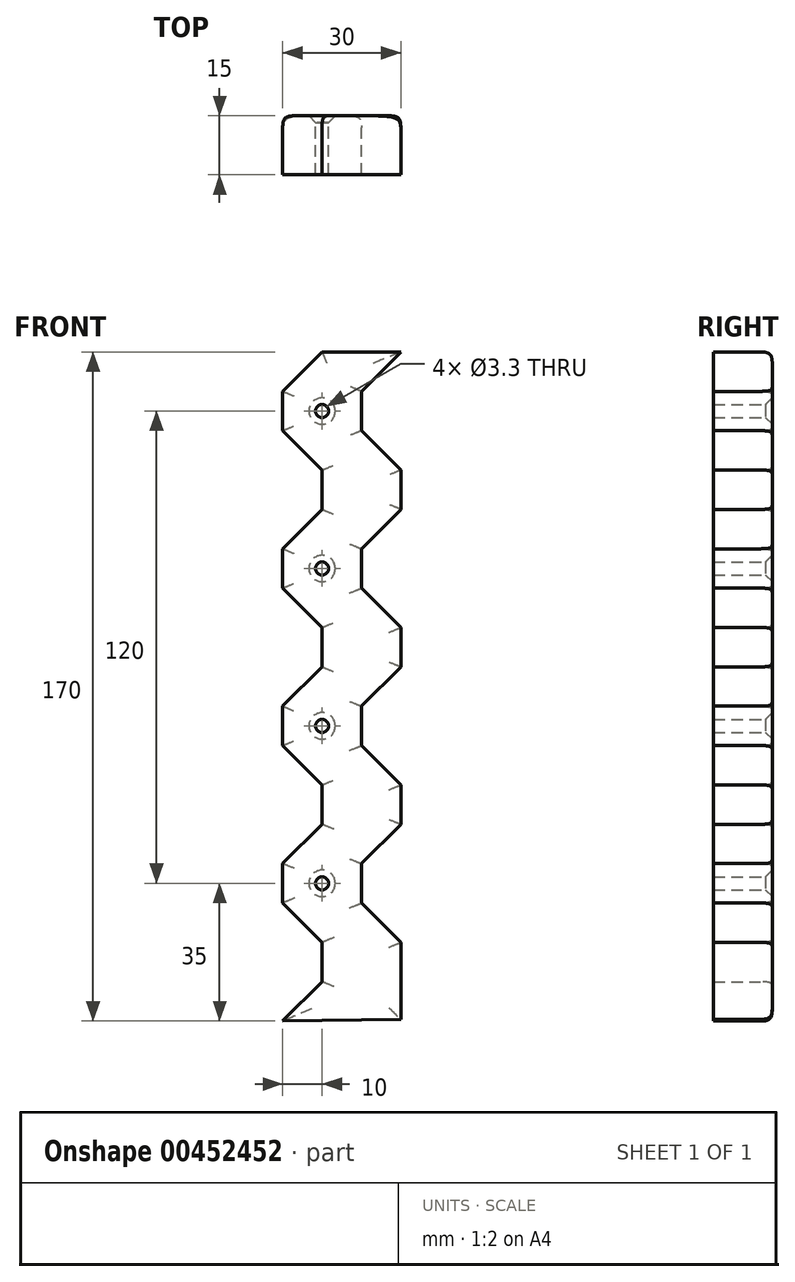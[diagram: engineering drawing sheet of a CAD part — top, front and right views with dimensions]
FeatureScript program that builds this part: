
annotation { "Feature Type Name" : "Feature", "Feature Type Description" : "" }
export const myFeature = defineFeature(function(context is Context, id is Id, definition is map)
    precondition{}
    {
        {
            var Q0;
            Q0=qCreatedBy(makeId("Front.planeOp"),FACE);
            var sketch = newSketch(context, id + "F0", { "sketchPlane" : qUnion([Q0])});
            skLineSegment(sketch, "E0", {"start": v(0, 0) * mm, "end": v(-5, 0) * mm});
            skLineSegment(sketch, "E1", {"start": v(-5, 0) * mm, "end": v(-15, 0) * mm});
            skLineSegment(sketch, "E2", {"start": v(0, 0) * mm, "end": v(5, 0) * mm});
            skLineSegment(sketch, "E3", {"start": v(5, 0) * mm, "end": v(15, 0) * mm});
            skLineSegment(sketch, "E4", {"start": v(-15, 0) * mm, "end": v(-15, -10) * mm});
            skLineSegment(sketch, "E5", {"start": v(-15, -10) * mm, "end": v(-15, -20) * mm});
            skLineSegment(sketch, "E6", {"start": v(-15, -20) * mm, "end": v(-15, -30) * mm});
            skLineSegment(sketch, "E7", {"start": v(-15, -30) * mm, "end": v(-15, -40) * mm});
            skLineSegment(sketch, "E8", {"start": v(-15, -40) * mm, "end": v(-15, -50) * mm});
            skLineSegment(sketch, "E9", {"start": v(-15, -60) * mm, "end": v(-15, -50) * mm});
            skLineSegment(sketch, "E10", {"start": v(-5, 0) * mm, "end": v(-5, -170) * mm});
            skLineSegment(sketch, "E11", {"start": v(-15, -60) * mm, "end": v(-15, -70) * mm});
            skLineSegment(sketch, "E12", {"start": v(-15, -70) * mm, "end": v(-15, -80) * mm});
            skLineSegment(sketch, "E13", {"start": v(-15, -80) * mm, "end": v(-15, -90) * mm});
            skLineSegment(sketch, "E14", {"start": v(-15, -90) * mm, "end": v(-15, -100) * mm});
            skLineSegment(sketch, "E15", {"start": v(-15, -100) * mm, "end": v(-15, -110) * mm});
            skLineSegment(sketch, "E16", {"start": v(-15, -110) * mm, "end": v(-15, -120) * mm});
            skLineSegment(sketch, "E17", {"start": v(-15, -120) * mm, "end": v(-15, -130) * mm});
            skLineSegment(sketch, "E18", {"start": v(-15, -130) * mm, "end": v(-15, -140) * mm});
            skLineSegment(sketch, "E19", {"start": v(-15, -140) * mm, "end": v(-15, -150) * mm});
            skLineSegment(sketch, "E20", {"start": v(-15, -150) * mm, "end": v(-15, -160) * mm});
            skLineSegment(sketch, "E21", {"start": v(-15, -160) * mm, "end": v(-15, -170) * mm});
            skLineSegment(sketch, "E22", {"start": v(5, 0) * mm, "end": v(5, -169.57) * mm});
            skLineSegment(sketch, "E23", {"start": v(15, 0) * mm, "end": v(15, -169.57) * mm});
            skLineSegment(sketch, "E24", {"start": v(-15, -10) * mm, "end": v(15, -10) * mm});
            skLineSegment(sketch, "E25", {"start": v(-15, -20) * mm, "end": v(15, -20) * mm});
            skLineSegment(sketch, "E26", {"start": v(-15, -30) * mm, "end": v(15, -30) * mm});
            skLineSegment(sketch, "E27", {"start": v(-15, -40) * mm, "end": v(15, -40) * mm});
            skLineSegment(sketch, "E28", {"start": v(-15, -50) * mm, "end": v(15, -50) * mm});
            skLineSegment(sketch, "E29", {"start": v(-15, -60) * mm, "end": v(15, -60) * mm});
            skLineSegment(sketch, "E30", {"start": v(-15, -70) * mm, "end": v(15, -70) * mm});
            skLineSegment(sketch, "E31", {"start": v(-15, -80) * mm, "end": v(15, -80) * mm});
            skLineSegment(sketch, "E32", {"start": v(-15, -90) * mm, "end": v(15, -90) * mm});
            skLineSegment(sketch, "E33", {"start": v(-15, -100) * mm, "end": v(15, -100) * mm});
            skLineSegment(sketch, "E34", {"start": v(-15, -110) * mm, "end": v(15, -110) * mm});
            skLineSegment(sketch, "E35", {"start": v(-15, -120) * mm, "end": v(15, -120) * mm});
            skLineSegment(sketch, "E36", {"start": v(-15, -130) * mm, "end": v(15, -130) * mm});
            skLineSegment(sketch, "E37", {"start": v(-15, -140) * mm, "end": v(15, -140) * mm});
            skLineSegment(sketch, "E38", {"start": v(-15, -150) * mm, "end": v(15, -150) * mm});
            skLineSegment(sketch, "E39", {"start": v(-15, -160) * mm, "end": v(15, -160) * mm});
            skLineSegment(sketch, "E40", {"start": v(-15, -170) * mm, "end": v(15, -169.57) * mm});
            skLineSegment(sketch, "E41", {"start": v(-5, 0) * mm, "end": v(-15, -10) * mm});
            skLineSegment(sketch, "E42", {"start": v(-5, -30) * mm, "end": v(-15, -20) * mm});
            skLineSegment(sketch, "E43", {"start": v(-5, -40) * mm, "end": v(-15, -50) * mm});
            skLineSegment(sketch, "E44", {"start": v(-5, -70) * mm, "end": v(-15, -60) * mm});
            skLineSegment(sketch, "E45", {"start": v(-15, -90) * mm, "end": v(-5, -80) * mm});
            skLineSegment(sketch, "E46", {"start": v(-15, -100) * mm, "end": v(-5, -110) * mm});
            skLineSegment(sketch, "E47", {"start": v(-5, -120) * mm, "end": v(-15, -130) * mm});
            skLineSegment(sketch, "E48", {"start": v(-5, -150) * mm, "end": v(-15, -140) * mm});
            skLineSegment(sketch, "E49", {"start": v(-5, -160) * mm, "end": v(-15, -170) * mm});
            skLineSegment(sketch, "E50", {"start": v(5, -140) * mm, "end": v(15, -150) * mm});
            skLineSegment(sketch, "E51", {"start": v(5, -130) * mm, "end": v(15, -120) * mm});
            skLineSegment(sketch, "E52", {"start": v(15, -160) * mm, "end": v(5, -169.57) * mm});
            skLineSegment(sketch, "E53", {"start": v(15, -110) * mm, "end": v(5, -100) * mm});
            skLineSegment(sketch, "E54", {"start": v(15, -80) * mm, "end": v(5, -90) * mm});
            skLineSegment(sketch, "E55", {"start": v(15, -70) * mm, "end": v(5, -60) * mm});
            skLineSegment(sketch, "E56", {"start": v(15, 0) * mm, "end": v(5, -10) * mm});
            skLineSegment(sketch, "E57", {"start": v(5, -20) * mm, "end": v(15, -30) * mm});
            skLineSegment(sketch, "E58", {"start": v(15, -40) * mm, "end": v(5, -50) * mm});
            skLineSegment(sketch, "E59", {"start": v(0, 0) * mm, "end": v(0, -169.78) * mm});
            skPoint(sketch, "E60.positionSnap0", {"position": v(-15, -15) * mm});
            skPoint(sketch, "E61.positionSnap0", {"position": v(-15, -55) * mm});
            skPoint(sketch, "E62.positionSnap0", {"position": v(-15, -95) * mm});
            skPoint(sketch, "E63.positionSnap0", {"position": v(-15, -135) * mm});
            skPoint(sketch, "E64", {"position": v(-5, -55) * mm});
            skPoint(sketch, "E65", {"position": v(-5, -15) * mm});
            skPoint(sketch, "E66", {"position": v(-5, -95) * mm});
            skPoint(sketch, "E67", {"position": v(-5, -135) * mm});
            skSolve(sketch);
        }
        {
            var Q0;
            {var subQ0=sQuery(id+"F0.wireOp",EDGE,"E41");Q0=makeQuery(id+"F0.imprint","IMPRINT",FACE,{"disambiguationData":[TD([[makeQuery(id+"F0.imprint","IMPRINT",EDGE,{"derivedFrom":subQ0}),1.0]])]});}
            var Q1;
            {var subQ0=sQuery(id+"F0.wireOp",EDGE,"E5");Q1=makeQuery(id+"F0.imprint","IMPRINT",FACE,{"disambiguationData":[TD([[makeQuery(id+"F0.imprint","IMPRINT",EDGE,{"derivedFrom":subQ0}),1.0]])]});}
            var Q2;
            {var subQ0=sQuery(id+"F0.wireOp",EDGE,"E42");Q2=makeQuery(id+"F0.imprint","IMPRINT",FACE,{"disambiguationData":[TD([[makeQuery(id+"F0.imprint","IMPRINT",EDGE,{"derivedFrom":subQ0}),-1.0]])]});}
            var Q3;
            {var subQ1=sQuery(id+"F0.wireOp",EDGE,"E10");var subQ3=sQuery(id+"F0.wireOp",EDGE,"E25");var subQ4=makeQuery(id+"F0.imprint","INTERSECT",VERTEX,{"derivedFrom":[subQ1,subQ3]});Q3=makeQuery(id+"F0.imprint","IMPRINT",FACE,{"disambiguationData":[TD([[makeQuery(id+"F0.imprint","IMPRINT",EDGE,{"disambiguationData":[TD([[subQ4,-1.0]])],"derivedFrom":subQ1}),1.0]])]});}
            var Q4;
            {var subQ0=sQuery(id+"F0.wireOp",EDGE,"E24");var subQ1=sQuery(id+"F0.wireOp",EDGE,"E10");var subQ2=makeQuery(id+"F0.imprint","INTERSECT",VERTEX,{"derivedFrom":[subQ1,subQ0]});Q4=makeQuery(id+"F0.imprint","IMPRINT",FACE,{"disambiguationData":[TD([[makeQuery(id+"F0.imprint","IMPRINT",EDGE,{"disambiguationData":[TD([[subQ2,-1.0]])],"derivedFrom":subQ1}),1.0]])]});}
            var Q5;
            {var subQ5=sQuery(id+"F0.wireOp",EDGE,"E0");Q5=makeQuery(id+"F0.imprint","IMPRINT",FACE,{"disambiguationData":[TD([[makeQuery(id+"F0.imprint","IMPRINT",EDGE,{"derivedFrom":subQ5}),1.0]])]});}
            var Q6;
            {var subQ0=sQuery(id+"F0.wireOp",EDGE,"E3");Q6=makeQuery(id+"F0.imprint","IMPRINT",FACE,{"disambiguationData":[TD([[makeQuery(id+"F0.imprint","IMPRINT",EDGE,{"derivedFrom":subQ0}),-1.0]])]});}
            var Q7;
            {var subQ0=sQuery(id+"F0.wireOp",EDGE,"E57");Q7=makeQuery(id+"F0.imprint","IMPRINT",FACE,{"disambiguationData":[TD([[makeQuery(id+"F0.imprint","IMPRINT",EDGE,{"derivedFrom":subQ0}),-1.0]])]});}
            var Q8;
            {var subQ0=sQuery(id+"F0.wireOp",EDGE,"E26");var subQ5=sQuery(id+"F0.wireOp",EDGE,"E22");var subQ6=makeQuery(id+"F0.imprint","INTERSECT",VERTEX,{"derivedFrom":[subQ5,subQ0]});Q8=makeQuery(id+"F0.imprint","IMPRINT",FACE,{"disambiguationData":[TD([[makeQuery(id+"F0.imprint","IMPRINT",EDGE,{"disambiguationData":[TD([[subQ6,-1.0]])],"derivedFrom":subQ5}),-1.0]])]});}
            var Q9;
            {var subQ0=sQuery(id+"F0.wireOp",EDGE,"E26");var subQ1=sQuery(id+"F0.wireOp",EDGE,"E22");var subQ2=makeQuery(id+"F0.imprint","INTERSECT",VERTEX,{"derivedFrom":[subQ1,subQ0]});Q9=makeQuery(id+"F0.imprint","IMPRINT",FACE,{"disambiguationData":[TD([[makeQuery(id+"F0.imprint","IMPRINT",EDGE,{"disambiguationData":[TD([[subQ2,-1.0]])],"derivedFrom":subQ1}),1.0]])]});}
            var Q10;
            {var subQ0=sQuery(id+"F0.wireOp",EDGE,"E58");Q10=makeQuery(id+"F0.imprint","IMPRINT",FACE,{"disambiguationData":[TD([[makeQuery(id+"F0.imprint","IMPRINT",EDGE,{"derivedFrom":subQ0}),-1.0]])]});}
            var Q11;
            {var subQ1=sQuery(id+"F0.wireOp",EDGE,"E10");var subQ3=sQuery(id+"F0.wireOp",EDGE,"E28");var subQ4=makeQuery(id+"F0.imprint","INTERSECT",VERTEX,{"derivedFrom":[subQ1,subQ3]});Q11=makeQuery(id+"F0.imprint","IMPRINT",FACE,{"disambiguationData":[TD([[makeQuery(id+"F0.imprint","IMPRINT",EDGE,{"disambiguationData":[TD([[subQ4,1.0]])],"derivedFrom":subQ1}),1.0]])]});}
            var Q12;
            {var subQ0=sQuery(id+"F0.wireOp",EDGE,"E43");Q12=makeQuery(id+"F0.imprint","IMPRINT",FACE,{"disambiguationData":[TD([[makeQuery(id+"F0.imprint","IMPRINT",EDGE,{"derivedFrom":subQ0}),1.0]])]});}
            var Q13;
            {var subQ0=sQuery(id+"F0.wireOp",EDGE,"E9");Q13=makeQuery(id+"F0.imprint","IMPRINT",FACE,{"disambiguationData":[TD([[makeQuery(id+"F0.imprint","IMPRINT",EDGE,{"derivedFrom":subQ0}),-1.0]])]});}
            var Q14;
            {var subQ0=sQuery(id+"F0.wireOp",EDGE,"E28");var subQ1=sQuery(id+"F0.wireOp",EDGE,"E10");var subQ2=makeQuery(id+"F0.imprint","INTERSECT",VERTEX,{"derivedFrom":[subQ1,subQ0]});Q14=makeQuery(id+"F0.imprint","IMPRINT",FACE,{"disambiguationData":[TD([[makeQuery(id+"F0.imprint","IMPRINT",EDGE,{"disambiguationData":[TD([[subQ2,-1.0]])],"derivedFrom":subQ1}),1.0]])]});}
            var Q15;
            {var subQ0=sQuery(id+"F0.wireOp",EDGE,"E55");Q15=makeQuery(id+"F0.imprint","IMPRINT",FACE,{"disambiguationData":[TD([[makeQuery(id+"F0.imprint","IMPRINT",EDGE,{"derivedFrom":subQ0}),1.0]])]});}
            var Q16;
            {var subQ1=sQuery(id+"F0.wireOp",EDGE,"E10");var subQ3=sQuery(id+"F0.wireOp",EDGE,"E29");var subQ4=makeQuery(id+"F0.imprint","INTERSECT",VERTEX,{"derivedFrom":[subQ1,subQ3]});Q16=makeQuery(id+"F0.imprint","IMPRINT",FACE,{"disambiguationData":[TD([[makeQuery(id+"F0.imprint","IMPRINT",EDGE,{"disambiguationData":[TD([[subQ4,-1.0]])],"derivedFrom":subQ1}),1.0]])]});}
            var Q17;
            {var subQ0=sQuery(id+"F0.wireOp",EDGE,"E44");Q17=makeQuery(id+"F0.imprint","IMPRINT",FACE,{"disambiguationData":[TD([[makeQuery(id+"F0.imprint","IMPRINT",EDGE,{"derivedFrom":subQ0}),-1.0]])]});}
            var Q18;
            {var subQ0=sQuery(id+"F0.wireOp",EDGE,"E30");var subQ5=sQuery(id+"F0.wireOp",EDGE,"E22");var subQ6=makeQuery(id+"F0.imprint","INTERSECT",VERTEX,{"derivedFrom":[subQ5,subQ0]});Q18=makeQuery(id+"F0.imprint","IMPRINT",FACE,{"disambiguationData":[TD([[makeQuery(id+"F0.imprint","IMPRINT",EDGE,{"disambiguationData":[TD([[subQ6,-1.0]])],"derivedFrom":subQ5}),-1.0]])]});}
            var Q19;
            {var subQ1=sQuery(id+"F0.wireOp",EDGE,"E10");var subQ3=sQuery(id+"F0.wireOp",EDGE,"E32");var subQ4=makeQuery(id+"F0.imprint","INTERSECT",VERTEX,{"derivedFrom":[subQ1,subQ3]});Q19=makeQuery(id+"F0.imprint","IMPRINT",FACE,{"disambiguationData":[TD([[makeQuery(id+"F0.imprint","IMPRINT",EDGE,{"disambiguationData":[TD([[subQ4,1.0]])],"derivedFrom":subQ1}),1.0]])]});}
            var Q20;
            {var subQ1=sQuery(id+"F0.wireOp",EDGE,"E10");var subQ3=sQuery(id+"F0.wireOp",EDGE,"E33");var subQ4=makeQuery(id+"F0.imprint","INTERSECT",VERTEX,{"derivedFrom":[subQ1,subQ3]});Q20=makeQuery(id+"F0.imprint","IMPRINT",FACE,{"disambiguationData":[TD([[makeQuery(id+"F0.imprint","IMPRINT",EDGE,{"disambiguationData":[TD([[subQ4,-1.0]])],"derivedFrom":subQ1}),1.0]])]});}
            var Q21;
            {var subQ0=sQuery(id+"F0.wireOp",EDGE,"E32");var subQ1=sQuery(id+"F0.wireOp",EDGE,"E10");var subQ2=makeQuery(id+"F0.imprint","INTERSECT",VERTEX,{"derivedFrom":[subQ1,subQ0]});Q21=makeQuery(id+"F0.imprint","IMPRINT",FACE,{"disambiguationData":[TD([[makeQuery(id+"F0.imprint","IMPRINT",EDGE,{"disambiguationData":[TD([[subQ2,-1.0]])],"derivedFrom":subQ1}),1.0]])]});}
            var Q22;
            {var subQ0=sQuery(id+"F0.wireOp",EDGE,"E34");var subQ5=sQuery(id+"F0.wireOp",EDGE,"E22");var subQ7=makeQuery(id+"F0.imprint","INTERSECT",VERTEX,{"derivedFrom":[subQ5,subQ0]});Q22=makeQuery(id+"F0.imprint","IMPRINT",FACE,{"disambiguationData":[TD([[makeQuery(id+"F0.imprint","IMPRINT",EDGE,{"disambiguationData":[TD([[subQ7,-1.0]])],"derivedFrom":subQ5}),-1.0]])]});}
            var Q23;
            {var subQ1=sQuery(id+"F0.wireOp",EDGE,"E10");var subQ3=sQuery(id+"F0.wireOp",EDGE,"E36");var subQ4=makeQuery(id+"F0.imprint","INTERSECT",VERTEX,{"derivedFrom":[subQ1,subQ3]});Q23=makeQuery(id+"F0.imprint","IMPRINT",FACE,{"disambiguationData":[TD([[makeQuery(id+"F0.imprint","IMPRINT",EDGE,{"disambiguationData":[TD([[subQ4,1.0]])],"derivedFrom":subQ1}),1.0]])]});}
            var Q24;
            {var subQ0=sQuery(id+"F0.wireOp",EDGE,"E36");var subQ1=sQuery(id+"F0.wireOp",EDGE,"E10");var subQ2=makeQuery(id+"F0.imprint","INTERSECT",VERTEX,{"derivedFrom":[subQ1,subQ0]});Q24=makeQuery(id+"F0.imprint","IMPRINT",FACE,{"disambiguationData":[TD([[makeQuery(id+"F0.imprint","IMPRINT",EDGE,{"disambiguationData":[TD([[subQ2,-1.0]])],"derivedFrom":subQ1}),1.0]])]});}
            var Q25;
            {var subQ1=sQuery(id+"F0.wireOp",EDGE,"E10");var subQ3=sQuery(id+"F0.wireOp",EDGE,"E37");var subQ4=makeQuery(id+"F0.imprint","INTERSECT",VERTEX,{"derivedFrom":[subQ1,subQ3]});Q25=makeQuery(id+"F0.imprint","IMPRINT",FACE,{"disambiguationData":[TD([[makeQuery(id+"F0.imprint","IMPRINT",EDGE,{"disambiguationData":[TD([[subQ4,-1.0]])],"derivedFrom":subQ1}),1.0]])]});}
            var Q26;
            {var subQ0=sQuery(id+"F0.wireOp",EDGE,"E45");Q26=makeQuery(id+"F0.imprint","IMPRINT",FACE,{"disambiguationData":[TD([[makeQuery(id+"F0.imprint","IMPRINT",EDGE,{"derivedFrom":subQ0}),-1.0]])]});}
            var Q27;
            {var subQ5=sQuery(id+"F0.wireOp",EDGE,"E14");Q27=makeQuery(id+"F0.imprint","IMPRINT",FACE,{"disambiguationData":[TD([[makeQuery(id+"F0.imprint","IMPRINT",EDGE,{"derivedFrom":subQ5}),1.0]])]});}
            var Q28;
            {var subQ0=sQuery(id+"F0.wireOp",EDGE,"E46");Q28=makeQuery(id+"F0.imprint","IMPRINT",FACE,{"disambiguationData":[TD([[makeQuery(id+"F0.imprint","IMPRINT",EDGE,{"derivedFrom":subQ0}),1.0]])]});}
            var Q29;
            {var subQ0=sQuery(id+"F0.wireOp",EDGE,"E47");Q29=makeQuery(id+"F0.imprint","IMPRINT",FACE,{"disambiguationData":[TD([[makeQuery(id+"F0.imprint","IMPRINT",EDGE,{"derivedFrom":subQ0}),1.0]])]});}
            var Q30;
            {var subQ0=sQuery(id+"F0.wireOp",EDGE,"E30");var subQ1=sQuery(id+"F0.wireOp",EDGE,"E22");var subQ2=makeQuery(id+"F0.imprint","INTERSECT",VERTEX,{"derivedFrom":[subQ1,subQ0]});Q30=makeQuery(id+"F0.imprint","IMPRINT",FACE,{"disambiguationData":[TD([[makeQuery(id+"F0.imprint","IMPRINT",EDGE,{"disambiguationData":[TD([[subQ2,-1.0]])],"derivedFrom":subQ1}),1.0]])]});}
            var Q31;
            {var subQ0=sQuery(id+"F0.wireOp",EDGE,"E54");Q31=makeQuery(id+"F0.imprint","IMPRINT",FACE,{"disambiguationData":[TD([[makeQuery(id+"F0.imprint","IMPRINT",EDGE,{"derivedFrom":subQ0}),-1.0]])]});}
            var Q32;
            {var subQ0=sQuery(id+"F0.wireOp",EDGE,"E53");Q32=makeQuery(id+"F0.imprint","IMPRINT",FACE,{"disambiguationData":[TD([[makeQuery(id+"F0.imprint","IMPRINT",EDGE,{"derivedFrom":subQ0}),1.0]])]});}
            var Q33;
            {var subQ0=sQuery(id+"F0.wireOp",EDGE,"E34");var subQ1=sQuery(id+"F0.wireOp",EDGE,"E22");var subQ2=makeQuery(id+"F0.imprint","INTERSECT",VERTEX,{"derivedFrom":[subQ1,subQ0]});Q33=makeQuery(id+"F0.imprint","IMPRINT",FACE,{"disambiguationData":[TD([[makeQuery(id+"F0.imprint","IMPRINT",EDGE,{"disambiguationData":[TD([[subQ2,-1.0]])],"derivedFrom":subQ1}),1.0]])]});}
            var Q34;
            {var subQ0=sQuery(id+"F0.wireOp",EDGE,"E51");Q34=makeQuery(id+"F0.imprint","IMPRINT",FACE,{"disambiguationData":[TD([[makeQuery(id+"F0.imprint","IMPRINT",EDGE,{"derivedFrom":subQ0}),1.0]])]});}
            var Q35;
            {var subQ0=sQuery(id+"F0.wireOp",EDGE,"E50");Q35=makeQuery(id+"F0.imprint","IMPRINT",FACE,{"disambiguationData":[TD([[makeQuery(id+"F0.imprint","IMPRINT",EDGE,{"derivedFrom":subQ0}),-1.0]])]});}
            var Q36;
            {var subQ5=sQuery(id+"F0.wireOp",EDGE,"E18");Q36=makeQuery(id+"F0.imprint","IMPRINT",FACE,{"disambiguationData":[TD([[makeQuery(id+"F0.imprint","IMPRINT",EDGE,{"derivedFrom":subQ5}),1.0]])]});}
            var Q37;
            {var subQ0=sQuery(id+"F0.wireOp",EDGE,"E48");Q37=makeQuery(id+"F0.imprint","IMPRINT",FACE,{"disambiguationData":[TD([[makeQuery(id+"F0.imprint","IMPRINT",EDGE,{"derivedFrom":subQ0}),-1.0]])]});}
            var Q38;
            {var subQ0=sQuery(id+"F0.wireOp",EDGE,"E38");var subQ5=sQuery(id+"F0.wireOp",EDGE,"E22");var subQ6=makeQuery(id+"F0.imprint","INTERSECT",VERTEX,{"derivedFrom":[subQ5,subQ0]});Q38=makeQuery(id+"F0.imprint","IMPRINT",FACE,{"disambiguationData":[TD([[makeQuery(id+"F0.imprint","IMPRINT",EDGE,{"disambiguationData":[TD([[subQ6,-1.0]])],"derivedFrom":subQ5}),-1.0]])]});}
            var Q39;
            {var subQ0=sQuery(id+"F0.wireOp",EDGE,"E49");Q39=makeQuery(id+"F0.imprint","IMPRINT",FACE,{"disambiguationData":[TD([[makeQuery(id+"F0.imprint","IMPRINT",EDGE,{"derivedFrom":subQ0}),1.0]])]});}
            var Q40;
            {var subQ0=sQuery(id+"F0.wireOp",EDGE,"E52");Q40=makeQuery(id+"F0.imprint","IMPRINT",FACE,{"disambiguationData":[TD([[makeQuery(id+"F0.imprint","IMPRINT",EDGE,{"derivedFrom":subQ0}),-1.0]])]});}
            var Q41;
            {var subQ0=sQuery(id+"F0.wireOp",EDGE,"E38");var subQ1=sQuery(id+"F0.wireOp",EDGE,"E22");var subQ2=makeQuery(id+"F0.imprint","INTERSECT",VERTEX,{"derivedFrom":[subQ1,subQ0]});Q41=makeQuery(id+"F0.imprint","IMPRINT",FACE,{"disambiguationData":[TD([[makeQuery(id+"F0.imprint","IMPRINT",EDGE,{"disambiguationData":[TD([[subQ2,-1.0]])],"derivedFrom":subQ1}),1.0]])]});}
            var Q42;
            {var subQ5=sQuery(id+"F0.wireOp",EDGE,"E52");Q42=makeQuery(id+"F0.imprint","IMPRINT",FACE,{"disambiguationData":[TD([[makeQuery(id+"F0.imprint","IMPRINT",EDGE,{"derivedFrom":subQ5}),1.0]])]});}
            var Q43;
            {var subQ0=sQuery(id+"F0.wireOp",EDGE,"E2");Q43=makeQuery(id+"F0.imprint","IMPRINT",FACE,{"disambiguationData":[TD([[makeQuery(id+"F0.imprint","IMPRINT",EDGE,{"derivedFrom":subQ0}),-1.0]])]});}
            var Q44;
            {var subQ0=sQuery(id+"F0.wireOp",EDGE,"E24");var subQ5=sQuery(id+"F0.wireOp",EDGE,"E59");var subQ6=makeQuery(id+"F0.imprint","INTERSECT",VERTEX,{"derivedFrom":[subQ0,subQ5]});Q44=makeQuery(id+"F0.imprint","IMPRINT",FACE,{"disambiguationData":[TD([[makeQuery(id+"F0.imprint","IMPRINT",EDGE,{"disambiguationData":[TD([[subQ6,-1.0]])],"derivedFrom":subQ5}),1.0]])]});}
            var Q45;
            {var subQ1=sQuery(id+"F0.wireOp",EDGE,"E22");var subQ3=sQuery(id+"F0.wireOp",EDGE,"E26");var subQ4=makeQuery(id+"F0.imprint","INTERSECT",VERTEX,{"derivedFrom":[subQ1,subQ3]});Q45=makeQuery(id+"F0.imprint","IMPRINT",FACE,{"disambiguationData":[TD([[makeQuery(id+"F0.imprint","IMPRINT",EDGE,{"disambiguationData":[TD([[subQ4,1.0]])],"derivedFrom":subQ3}),1.0]])]});}
            var Q46;
            {var subQ0=sQuery(id+"F0.wireOp",EDGE,"E26");var subQ5=sQuery(id+"F0.wireOp",EDGE,"E59");var subQ6=makeQuery(id+"F0.imprint","INTERSECT",VERTEX,{"derivedFrom":[subQ0,subQ5]});Q46=makeQuery(id+"F0.imprint","IMPRINT",FACE,{"disambiguationData":[TD([[makeQuery(id+"F0.imprint","IMPRINT",EDGE,{"disambiguationData":[TD([[subQ6,-1.0]])],"derivedFrom":subQ5}),-1.0]])]});}
            var Q47;
            {var subQ1=sQuery(id+"F0.wireOp",EDGE,"E22");var subQ3=sQuery(id+"F0.wireOp",EDGE,"E27");var subQ4=makeQuery(id+"F0.imprint","INTERSECT",VERTEX,{"derivedFrom":[subQ1,subQ3]});Q47=makeQuery(id+"F0.imprint","IMPRINT",FACE,{"disambiguationData":[TD([[makeQuery(id+"F0.imprint","IMPRINT",EDGE,{"disambiguationData":[TD([[subQ4,1.0]])],"derivedFrom":subQ3}),-1.0]])]});}
            var Q48;
            {var subQ3=sQuery(id+"F0.wireOp",EDGE,"E28");var subQ5=sQuery(id+"F0.wireOp",EDGE,"E59");var subQ6=makeQuery(id+"F0.imprint","INTERSECT",VERTEX,{"derivedFrom":[subQ3,subQ5]});Q48=makeQuery(id+"F0.imprint","IMPRINT",FACE,{"disambiguationData":[TD([[makeQuery(id+"F0.imprint","IMPRINT",EDGE,{"disambiguationData":[TD([[subQ6,-1.0]])],"derivedFrom":subQ5}),1.0]])]});}
            var Q49;
            {var subQ1=sQuery(id+"F0.wireOp",EDGE,"E22");var subQ3=sQuery(id+"F0.wireOp",EDGE,"E30");var subQ4=makeQuery(id+"F0.imprint","INTERSECT",VERTEX,{"derivedFrom":[subQ1,subQ3]});Q49=makeQuery(id+"F0.imprint","IMPRINT",FACE,{"disambiguationData":[TD([[makeQuery(id+"F0.imprint","IMPRINT",EDGE,{"disambiguationData":[TD([[subQ4,1.0]])],"derivedFrom":subQ3}),1.0]])]});}
            var Q50;
            {var subQ0=sQuery(id+"F0.wireOp",EDGE,"E30");var subQ5=sQuery(id+"F0.wireOp",EDGE,"E59");var subQ6=makeQuery(id+"F0.imprint","INTERSECT",VERTEX,{"derivedFrom":[subQ0,subQ5]});Q50=makeQuery(id+"F0.imprint","IMPRINT",FACE,{"disambiguationData":[TD([[makeQuery(id+"F0.imprint","IMPRINT",EDGE,{"disambiguationData":[TD([[subQ6,-1.0]])],"derivedFrom":subQ5}),-1.0]])]});}
            var Q51;
            {var subQ3=sQuery(id+"F0.wireOp",EDGE,"E32");var subQ5=sQuery(id+"F0.wireOp",EDGE,"E59");var subQ6=makeQuery(id+"F0.imprint","INTERSECT",VERTEX,{"derivedFrom":[subQ3,subQ5]});Q51=makeQuery(id+"F0.imprint","IMPRINT",FACE,{"disambiguationData":[TD([[makeQuery(id+"F0.imprint","IMPRINT",EDGE,{"disambiguationData":[TD([[subQ6,-1.0]])],"derivedFrom":subQ5}),1.0]])]});}
            var Q52;
            {var subQ1=sQuery(id+"F0.wireOp",EDGE,"E22");var subQ3=sQuery(id+"F0.wireOp",EDGE,"E34");var subQ4=makeQuery(id+"F0.imprint","INTERSECT",VERTEX,{"derivedFrom":[subQ1,subQ3]});Q52=makeQuery(id+"F0.imprint","IMPRINT",FACE,{"disambiguationData":[TD([[makeQuery(id+"F0.imprint","IMPRINT",EDGE,{"disambiguationData":[TD([[subQ4,1.0]])],"derivedFrom":subQ3}),1.0]])]});}
            var Q53;
            {var subQ0=sQuery(id+"F0.wireOp",EDGE,"E34");var subQ5=sQuery(id+"F0.wireOp",EDGE,"E59");var subQ6=makeQuery(id+"F0.imprint","INTERSECT",VERTEX,{"derivedFrom":[subQ0,subQ5]});Q53=makeQuery(id+"F0.imprint","IMPRINT",FACE,{"disambiguationData":[TD([[makeQuery(id+"F0.imprint","IMPRINT",EDGE,{"disambiguationData":[TD([[subQ6,-1.0]])],"derivedFrom":subQ5}),-1.0]])]});}
            var Q54;
            {var subQ1=sQuery(id+"F0.wireOp",EDGE,"E22");var subQ3=sQuery(id+"F0.wireOp",EDGE,"E35");var subQ4=makeQuery(id+"F0.imprint","INTERSECT",VERTEX,{"derivedFrom":[subQ1,subQ3]});Q54=makeQuery(id+"F0.imprint","IMPRINT",FACE,{"disambiguationData":[TD([[makeQuery(id+"F0.imprint","IMPRINT",EDGE,{"disambiguationData":[TD([[subQ4,1.0]])],"derivedFrom":subQ3}),-1.0]])]});}
            var Q55;
            {var subQ3=sQuery(id+"F0.wireOp",EDGE,"E36");var subQ5=sQuery(id+"F0.wireOp",EDGE,"E59");var subQ7=makeQuery(id+"F0.imprint","INTERSECT",VERTEX,{"derivedFrom":[subQ3,subQ5]});Q55=makeQuery(id+"F0.imprint","IMPRINT",FACE,{"disambiguationData":[TD([[makeQuery(id+"F0.imprint","IMPRINT",EDGE,{"disambiguationData":[TD([[subQ7,-1.0]])],"derivedFrom":subQ5}),1.0]])]});}
            var Q56;
            {var subQ1=sQuery(id+"F0.wireOp",EDGE,"E22");var subQ3=sQuery(id+"F0.wireOp",EDGE,"E38");var subQ4=makeQuery(id+"F0.imprint","INTERSECT",VERTEX,{"derivedFrom":[subQ1,subQ3]});Q56=makeQuery(id+"F0.imprint","IMPRINT",FACE,{"disambiguationData":[TD([[makeQuery(id+"F0.imprint","IMPRINT",EDGE,{"disambiguationData":[TD([[subQ4,1.0]])],"derivedFrom":subQ3}),1.0]])]});}
            var Q57;
            {var subQ0=sQuery(id+"F0.wireOp",EDGE,"E38");var subQ5=sQuery(id+"F0.wireOp",EDGE,"E59");var subQ6=makeQuery(id+"F0.imprint","INTERSECT",VERTEX,{"derivedFrom":[subQ0,subQ5]});Q57=makeQuery(id+"F0.imprint","IMPRINT",FACE,{"disambiguationData":[TD([[makeQuery(id+"F0.imprint","IMPRINT",EDGE,{"disambiguationData":[TD([[subQ6,-1.0]])],"derivedFrom":subQ5}),-1.0]])]});}
            var Q58;
            {var subQ3=sQuery(id+"F0.wireOp",EDGE,"E40");var subQ5=sQuery(id+"F0.wireOp",EDGE,"E59");var subQ7=makeQuery(id+"F0.imprint","INTERSECT",VERTEX,{"derivedFrom":[subQ3,subQ5]});Q58=makeQuery(id+"F0.imprint","IMPRINT",FACE,{"disambiguationData":[TD([[makeQuery(id+"F0.imprint","IMPRINT",EDGE,{"disambiguationData":[TD([[subQ7,1.0]])],"derivedFrom":subQ3}),1.0]])]});}
            var Q59;
            {var subQ1=sQuery(id+"F0.wireOp",EDGE,"E22");var subQ3=sQuery(id+"F0.wireOp",EDGE,"E31");var subQ4=makeQuery(id+"F0.imprint","INTERSECT",VERTEX,{"derivedFrom":[subQ1,subQ3]});Q59=makeQuery(id+"F0.imprint","IMPRINT",FACE,{"disambiguationData":[TD([[makeQuery(id+"F0.imprint","IMPRINT",EDGE,{"disambiguationData":[TD([[subQ4,1.0]])],"derivedFrom":subQ3}),-1.0]])]});}
            extrude(context, id + "F1", {"entities" : qUnion([Q0, Q1, Q2, Q3, Q4, Q5, Q6, Q7, Q8, Q9, Q10, Q11, Q12, Q13, Q14, Q15, Q16, Q17, Q18, Q19, Q20, Q21, Q22, Q23, Q24, Q25, Q26, Q27, Q28, Q29, Q30, Q31, Q32, Q33, Q34, Q35, Q36, Q37, Q38, Q39, Q40, Q41, Q42, Q43, Q44, Q45, Q46, Q47, Q48, Q49, Q50, Q51, Q52, Q53, Q54, Q55, Q56, Q57, Q58, Q59]), "depth" : 15 * mm});
        }
        {
            var Q0;
            Q0=makeQuery(id+"F1.opExtrude","CAP_FACE",FACE,{"disambiguationData":[OSD([sQuery(id+"F0.wireOp",EDGE,"E0"),sQuery(id+"F0.wireOp",EDGE,"E2"),sQuery(id+"F0.wireOp",EDGE,"E3"),sQuery(id+"F0.wireOp",EDGE,"E5"),sQuery(id+"F0.wireOp",EDGE,"E9"),sQuery(id+"F0.wireOp",EDGE,"E10"),sQuery(id+"F0.wireOp",EDGE,"E14"),sQuery(id+"F0.wireOp",EDGE,"E18"),sQuery(id+"F0.wireOp",EDGE,"E22"),sQuery(id+"F0.wireOp",EDGE,"E23"),sQuery(id+"F0.wireOp",EDGE,"E40"),sQuery(id+"F0.wireOp",EDGE,"E41"),sQuery(id+"F0.wireOp",EDGE,"E42"),sQuery(id+"F0.wireOp",EDGE,"E43"),sQuery(id+"F0.wireOp",EDGE,"E44"),sQuery(id+"F0.wireOp",EDGE,"E45"),sQuery(id+"F0.wireOp",EDGE,"E46"),sQuery(id+"F0.wireOp",EDGE,"E47"),sQuery(id+"F0.wireOp",EDGE,"E48"),sQuery(id+"F0.wireOp",EDGE,"E49"),sQuery(id+"F0.wireOp",EDGE,"E50"),sQuery(id+"F0.wireOp",EDGE,"E51"),sQuery(id+"F0.wireOp",EDGE,"E53"),sQuery(id+"F0.wireOp",EDGE,"E54"),sQuery(id+"F0.wireOp",EDGE,"E55"),sQuery(id+"F0.wireOp",EDGE,"E56"),sQuery(id+"F0.wireOp",EDGE,"E57"),sQuery(id+"F0.wireOp",EDGE,"E58")])],"isStart":true});
            fillet(context, id + "F2", {"entities" : qUnion([Q0]), "radius" : 3 * mm, "tangentPropagation" : true, "rho" : 0.6, "crossSection" : FilletCrossSection.CONIC, "allowEdgeOverflow" : false});
        }
        {
            var Q0;
            Q0=sQuery(id+"F0.wireOp",VERTEX,"E67");
            var Q1;
            Q1=sQuery(id+"F0.wireOp",VERTEX,"E66");
            var Q2;
            Q2=sQuery(id+"F0.wireOp",VERTEX,"E64");
            var Q3;
            Q3=sQuery(id+"F0.wireOp",VERTEX,"E65");
            var Q4;
            Q4=makeQuery(id+"F1.opExtrude","SWEPT_BODY",BODY,{"disambiguationData":[OSD([sQuery(id+"F0.wireOp",EDGE,"E0"),sQuery(id+"F0.wireOp",EDGE,"E2"),sQuery(id+"F0.wireOp",EDGE,"E3"),sQuery(id+"F0.wireOp",EDGE,"E5"),sQuery(id+"F0.wireOp",EDGE,"E9"),sQuery(id+"F0.wireOp",EDGE,"E10"),sQuery(id+"F0.wireOp",EDGE,"E14"),sQuery(id+"F0.wireOp",EDGE,"E18"),sQuery(id+"F0.wireOp",EDGE,"E22"),sQuery(id+"F0.wireOp",EDGE,"E23"),sQuery(id+"F0.wireOp",EDGE,"E40"),sQuery(id+"F0.wireOp",EDGE,"E41"),sQuery(id+"F0.wireOp",EDGE,"E42"),sQuery(id+"F0.wireOp",EDGE,"E43"),sQuery(id+"F0.wireOp",EDGE,"E44"),sQuery(id+"F0.wireOp",EDGE,"E45"),sQuery(id+"F0.wireOp",EDGE,"E46"),sQuery(id+"F0.wireOp",EDGE,"E47"),sQuery(id+"F0.wireOp",EDGE,"E48"),sQuery(id+"F0.wireOp",EDGE,"E49"),sQuery(id+"F0.wireOp",EDGE,"E50"),sQuery(id+"F0.wireOp",EDGE,"E51"),sQuery(id+"F0.wireOp",EDGE,"E53"),sQuery(id+"F0.wireOp",EDGE,"E54"),sQuery(id+"F0.wireOp",EDGE,"E55"),sQuery(id+"F0.wireOp",EDGE,"E56"),sQuery(id+"F0.wireOp",EDGE,"E57"),sQuery(id+"F0.wireOp",EDGE,"E58")])]});
            hole(context, id + "F3", {"style" : HoleStyle.C_SINK, "endStyle" : HoleEndStyle.THROUGH, "oppositeDirection" : true, "standardTappedOrClearance" : lookupTablePath({ "standard" : "ISO", "fit" : "Normal", "size" : "M3", "type" : "Clearance" }), "standardBlindInLast" : lookupTablePath({ "fit" : "Standard", "standard" : "ISO", "size" : "M3", "type" : "Clearance" }), "holeDiameter" : 3.3 * mm, "cSinkDiameter" : 6.72 * mm, "cSinkAngle" : 90 * degree, "isTappedThrough" : true, "tappedDepth" : 12 * mm, "tapClearance" : 3, "startFromSketch" : true, "locations" : qUnion([Q0, Q1, Q2, Q3]), "scope" : qUnion([Q4])});
        }
    });
